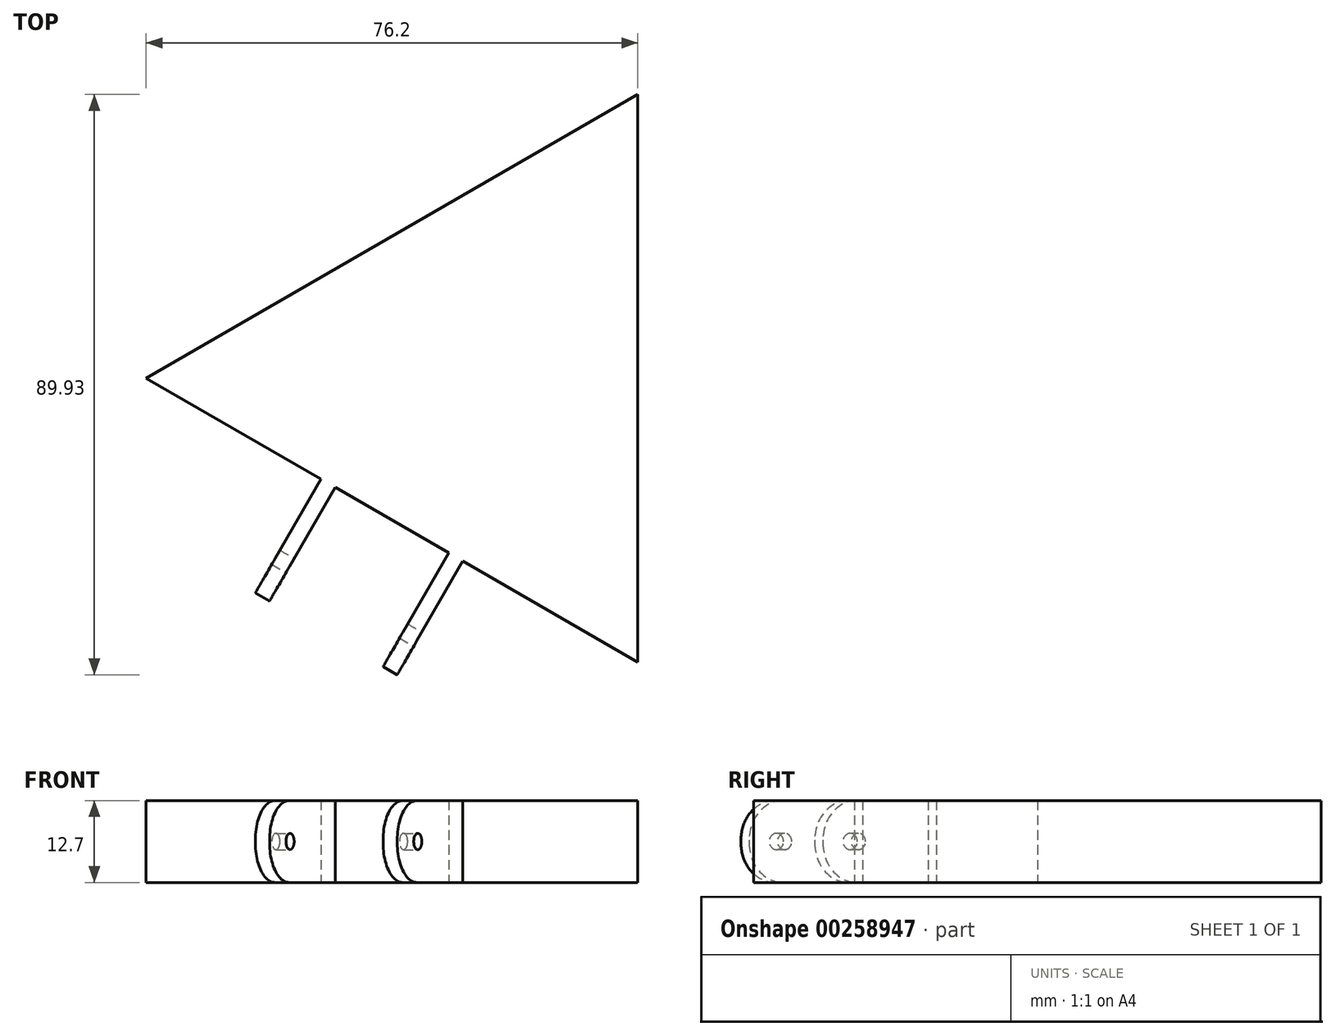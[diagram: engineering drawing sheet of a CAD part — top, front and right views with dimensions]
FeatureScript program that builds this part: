
annotation { "Feature Type Name" : "Feature", "Feature Type Description" : "" }
export const myFeature = defineFeature(function(context is Context, id is Id, definition is map)
    precondition{}
    {
        {
            var Q0;
            Q0=qCreatedBy(makeId("Top.planeOp"),FACE);
            var sketch = newSketch(context, id + "F0", { "sketchPlane" : qUnion([Q0])});
            skCircle(sketch, "E0.cCircle", {"center": v(0, 0) * mm, "radius": 25.4 * mm, "construction": true});
            skLineSegment(sketch, "E0.0", {"start": v(25.4, 44) * mm, "end": v(25.4, -44) * mm});
            skLineSegment(sketch, "E0.1", {"start": v(25.4, -44) * mm, "end": v(-50.8, 0) * mm});
            skLineSegment(sketch, "E0.2", {"start": v(-50.8, 0) * mm, "end": v(25.4, 44) * mm});
            skPoint(sketch, "E0.0.midPoint", {"position": v(25.4, 0) * mm});
            skSolve(sketch);
        }
        {
            var Q0;
            Q0 = qSketchRegion(id + "F0", true);
            extrude(context, id + "F1", {"entities" : qUnion([Q0]), "depth" : 12.7 * mm});
        }
        {
            var Q0;
            Q0=makeQuery(id+"F1.opExtrude","SWEPT_FACE",FACE,{"disambiguationData":[OSD([sQuery(id+"F0.wireOp",EDGE,"E0.1")])]});
            var sketch = newSketch(context, id + "F2", { "sketchPlane" : qUnion([Q0])});
            skLineSegment(sketch, "E1", {"start": v(0, 12.7) * mm, "end": v(0, 0) * mm, "construction": true});
            skLineSegment(sketch, "E2.bottom", {"start": v(10.16, 12.7) * mm, "end": v(12.7, 12.7) * mm});
            skLineSegment(sketch, "E2.top", {"start": v(10.16, 0) * mm, "end": v(12.7, 0) * mm});
            skLineSegment(sketch, "E2.left", {"start": v(10.16, 12.7) * mm, "end": v(10.16, 0) * mm});
            skLineSegment(sketch, "E2.right", {"start": v(12.7, 12.7) * mm, "end": v(12.7, 0) * mm});
            skLineSegment(sketch, "E3.bottom", {"start": v(-12.7, 12.7) * mm, "end": v(-10.16, 12.7) * mm});
            skLineSegment(sketch, "E3.top", {"start": v(-12.7, 0) * mm, "end": v(-10.16, 0) * mm});
            skLineSegment(sketch, "E3.left", {"start": v(-12.7, 12.7) * mm, "end": v(-12.7, 0) * mm});
            skLineSegment(sketch, "E3.right", {"start": v(-10.16, 12.7) * mm, "end": v(-10.16, 0) * mm});
            skSolve(sketch);
        }
        {
            var Q0;
            Q0 = qSketchRegion(id + "F2", true);
            extrude(context, id + "F3", {"entities" : qUnion([Q0]), "operationType" : NewBodyOperationType.ADD, "depth" : 20.32 * mm});
        }
        {
            var Q0;
            Q0=makeQuery(id+"F3.opExtrude","SWEPT_FACE",FACE,{"disambiguationData":[OSD([sQuery(id+"F2.wireOp",EDGE,"E2.right")])]});
            var sketch = newSketch(context, id + "F4", { "sketchPlane" : qUnion([Q0])});
            skCircle(sketch, "E4", {"center": v(-39.37, 6.35) * mm, "radius": 1.27 * mm});
            skLineSegment(sketch, "E5.bottom", {"start": v(-45.72, 12.7) * mm, "end": v(-33.02, 12.7) * mm, "construction": true});
            skLineSegment(sketch, "E5.top", {"start": v(-45.72, 0) * mm, "end": v(-33.02, 0) * mm, "construction": true});
            skLineSegment(sketch, "E5.left", {"start": v(-45.72, 12.7) * mm, "end": v(-45.72, 0) * mm, "construction": true});
            skLineSegment(sketch, "E5.right", {"start": v(-33.02, 12.7) * mm, "end": v(-33.02, 0) * mm, "construction": true});
            skLineSegment(sketch, "E6", {"start": v(-45.72, 12.7) * mm, "end": v(-33.02, 0) * mm, "construction": true});
            skLineSegment(sketch, "E7", {"start": v(-45.72, 0) * mm, "end": v(-33.02, 12.7) * mm, "construction": true});
            skSolve(sketch);
        }
        {
            var Q0;
            Q0 = qSketchRegion(id + "F4", true);
            extrude(context, id + "F5", {"entities" : qUnion([Q0]), "operationType" : NewBodyOperationType.REMOVE, "oppositeDirection" : true, "depth" : 39.14 * mm});
        }
        {
            var Q0;
            Q0=makeQuery(id+"F3.opExtrude","CAP_EDGE",EDGE,{"disambiguationData":[OSD([sQuery(id+"F2.wireOp",EDGE,"E3.top")])],"isStart":false});
            var Q1;
            Q1=makeQuery(id+"F3.opExtrude","CAP_EDGE",EDGE,{"disambiguationData":[OSD([sQuery(id+"F2.wireOp",EDGE,"E3.bottom")])],"isStart":false});
            var Q2;
            Q2=makeQuery(id+"F3.opExtrude","CAP_EDGE",EDGE,{"disambiguationData":[OSD([sQuery(id+"F2.wireOp",EDGE,"E2.bottom")])],"isStart":false});
            var Q3;
            Q3=makeQuery(id+"F3.opExtrude","CAP_EDGE",EDGE,{"disambiguationData":[OSD([sQuery(id+"F2.wireOp",EDGE,"E2.top")])],"isStart":false});
            fillet(context, id + "F6", {"entities" : qUnion([Q0, Q1, Q2, Q3]), "radius" : 6.1 * mm, "tangentPropagation" : true, "allowEdgeOverflow" : false});
        }
    });
